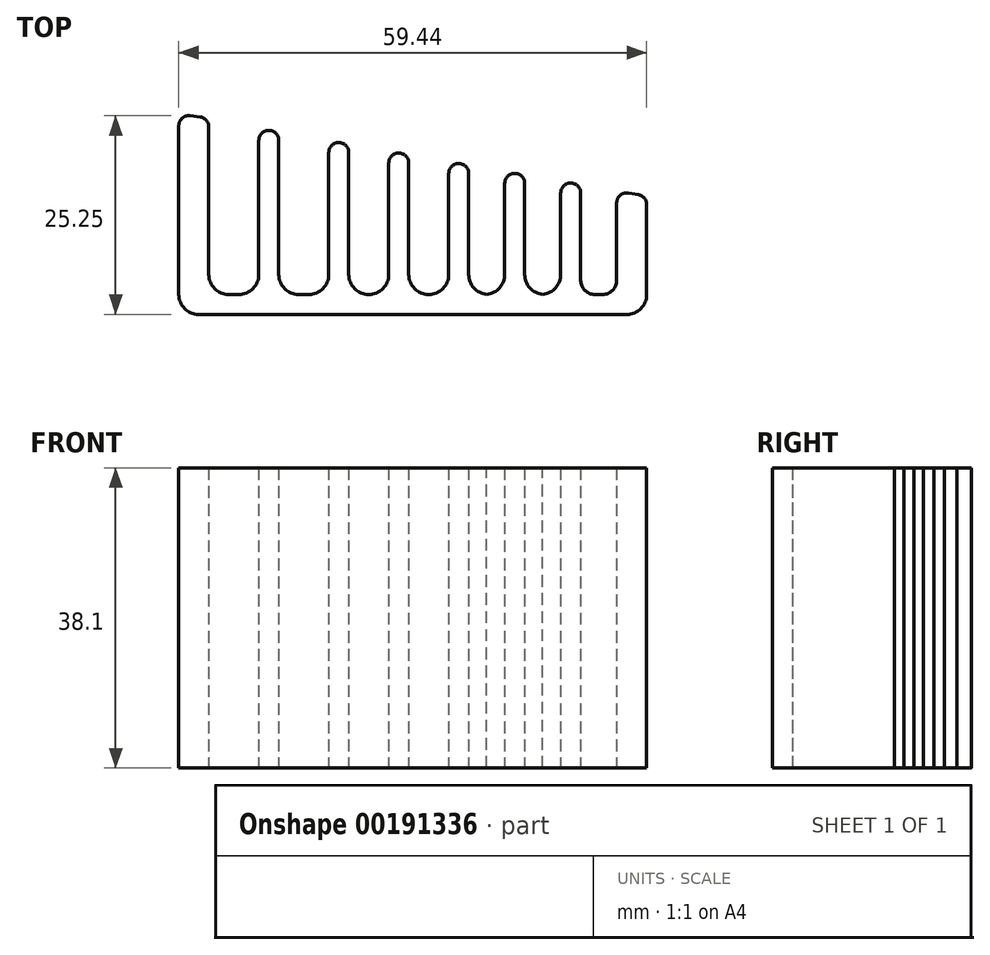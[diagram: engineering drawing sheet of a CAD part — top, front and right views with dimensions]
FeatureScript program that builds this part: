
annotation { "Feature Type Name" : "Feature", "Feature Type Description" : "" }
export const myFeature = defineFeature(function(context is Context, id is Id, definition is map)
    precondition{}
    {
        {
            var Q0;
            Q0=qCreatedBy(makeId("Top.planeOp"),FACE);
            var sketch = newSketch(context, id + "F0", { "sketchPlane" : qUnion([Q0])});
            skLineSegment(sketch, "E0", {"start": v(-36.35, 0) * mm, "end": v(36.35, 0) * mm});
            skPoint(sketch, "E1", {"position": v(0, 0) * mm});
            skLineSegment(sketch, "E2", {"start": v(-36.35, 0) * mm, "end": v(-36.35, 25.4) * mm});
            skLineSegment(sketch, "E3", {"start": v(36.35, 0) * mm, "end": v(36.35, 12.7) * mm});
            skPoint(sketch, "E4", {"position": v(-32.54, 24.98) * mm});
            skLineSegment(sketch, "E5", {"start": v(-36.35, 25.4) * mm, "end": v(-32.54, 24.98) * mm});
            skLineSegment(sketch, "E6", {"start": v(-32.54, 24.98) * mm, "end": v(-32.54, 2.54) * mm});
            skLineSegment(sketch, "E7", {"start": v(-36.35, 25.4) * mm, "end": v(36.35, 12.7) * mm, "construction": true});
            skLineSegment(sketch, "E8", {"start": v(-36.35, 2.54) * mm, "end": v(36.35, 2.54) * mm, "construction": true});
            skLineSegment(sketch, "E9", {"start": v(-26.19, 2.54) * mm, "end": v(-26.19, 23.63) * mm});
            skLineSegment(sketch, "E10", {"start": v(-26.19, 23.63) * mm, "end": v(-23.65, 23.18) * mm});
            skLineSegment(sketch, "E11", {"start": v(-23.65, 23.18) * mm, "end": v(-23.65, 2.54) * mm});
            skLineSegment(sketch, "E12", {"start": v(-23.65, 2.54) * mm, "end": v(-17.3, 2.54) * mm});
            skLineSegment(sketch, "E13", {"start": v(-17.3, 2.54) * mm, "end": v(-17.3, 22.07) * mm});
            skLineSegment(sketch, "E14", {"start": v(-17.3, 22.07) * mm, "end": v(-14.76, 21.63) * mm});
            skLineSegment(sketch, "E15", {"start": v(-14.76, 21.63) * mm, "end": v(-14.76, 2.54) * mm});
            skLineSegment(sketch, "E16", {"start": v(-14.76, 2.54) * mm, "end": v(-9.68, 2.54) * mm});
            skLineSegment(sketch, "E17", {"start": v(-9.68, 2.54) * mm, "end": v(-9.68, 20.74) * mm});
            skLineSegment(sketch, "E18", {"start": v(-9.68, 20.74) * mm, "end": v(-7.14, 20.3) * mm});
            skLineSegment(sketch, "E19", {"start": v(-7.14, 20.3) * mm, "end": v(-7.14, 2.54) * mm});
            skLineSegment(sketch, "E20", {"start": v(-7.14, 2.54) * mm, "end": v(-2.06, 2.54) * mm});
            skLineSegment(sketch, "E21", {"start": v(-2.06, 2.54) * mm, "end": v(-2.06, 19.4) * mm});
            skLineSegment(sketch, "E22", {"start": v(-2.06, 19.4) * mm, "end": v(0.48, 18.97) * mm});
            skLineSegment(sketch, "E23", {"start": v(0.48, 18.97) * mm, "end": v(0.48, 2.54) * mm});
            skLineSegment(sketch, "E24", {"start": v(0.48, 2.54) * mm, "end": v(5.05, 2.54) * mm});
            skLineSegment(sketch, "E25", {"start": v(5.05, 2.54) * mm, "end": v(5.05, 18.17) * mm});
            skLineSegment(sketch, "E26", {"start": v(5.05, 18.17) * mm, "end": v(7.6, 17.72) * mm});
            skLineSegment(sketch, "E27", {"start": v(7.6, 17.72) * mm, "end": v(7.6, 2.54) * mm});
            skLineSegment(sketch, "E28", {"start": v(7.6, 2.54) * mm, "end": v(12.17, 2.54) * mm});
            skLineSegment(sketch, "E29", {"start": v(12.17, 2.54) * mm, "end": v(12.17, 16.92) * mm});
            skLineSegment(sketch, "E30", {"start": v(12.17, 16.92) * mm, "end": v(14.7, 16.48) * mm});
            skLineSegment(sketch, "E31", {"start": v(14.7, 16.48) * mm, "end": v(14.7, 2.54) * mm});
            skLineSegment(sketch, "E32", {"start": v(14.7, 2.54) * mm, "end": v(19.28, 2.54) * mm});
            skLineSegment(sketch, "E33", {"start": v(19.28, 2.54) * mm, "end": v(19.28, 15.68) * mm});
            skLineSegment(sketch, "E34", {"start": v(19.28, 15.68) * mm, "end": v(23.09, 15.02) * mm});
            skLineSegment(sketch, "E35", {"start": v(23.09, 15.02) * mm, "end": v(23.09, 2.54) * mm});
            skLineSegment(sketch, "E36", {"start": v(23.09, 2.54) * mm, "end": v(26.8, 2.54) * mm});
            skLineSegment(sketch, "E37", {"start": v(26.8, 2.54) * mm, "end": v(26.8, 14.37) * mm});
            skLineSegment(sketch, "E38", {"start": v(26.8, 14.37) * mm, "end": v(29.34, 13.92) * mm});
            skLineSegment(sketch, "E39", {"start": v(29.34, 13.92) * mm, "end": v(29.34, 2.54) * mm});
            skLineSegment(sketch, "E40", {"start": v(29.34, 2.54) * mm, "end": v(32.54, 2.54) * mm});
            skLineSegment(sketch, "E41", {"start": v(32.54, 2.54) * mm, "end": v(32.54, 13.37) * mm});
            skLineSegment(sketch, "E42", {"start": v(32.54, 13.37) * mm, "end": v(36.35, 12.7) * mm});
            skLineSegment(sketch, "E43", {"start": v(-26.19, 2.54) * mm, "end": v(-32.54, 2.54) * mm});
            skSolve(sketch);
        }
        {
            var Q0;
            Q0=qSketchRegion(id+"F0",true);
            extrude(context, id + "F1", {"entities" : qUnion([Q0]), "depth" : 38.1 * mm});
        }
        {
            var Q0;
            Q0=makeQuery(id+"F1.opExtrude","SWEPT_EDGE",EDGE,{"disambiguationData":[OSD([sQuery(id+"F0.wireOp",EDGE,"E6"),sQuery(id+"F0.wireOp",EDGE,"E43")])]});
            var Q1;
            Q1=makeQuery(id+"F1.opExtrude","SWEPT_EDGE",EDGE,{"disambiguationData":[OSD([sQuery(id+"F0.wireOp",EDGE,"E9"),sQuery(id+"F0.wireOp",EDGE,"E43")])]});
            var Q2;
            Q2=makeQuery(id+"F1.opExtrude","SWEPT_EDGE",EDGE,{"disambiguationData":[OSD([sQuery(id+"F0.wireOp",EDGE,"E11"),sQuery(id+"F0.wireOp",EDGE,"E12")])]});
            var Q3;
            Q3=makeQuery(id+"F1.opExtrude","SWEPT_EDGE",EDGE,{"disambiguationData":[OSD([sQuery(id+"F0.wireOp",EDGE,"E12"),sQuery(id+"F0.wireOp",EDGE,"E13")])]});
            var Q4;
            Q4=makeQuery(id+"F1.opExtrude","SWEPT_EDGE",EDGE,{"disambiguationData":[OSD([sQuery(id+"F0.wireOp",EDGE,"E15"),sQuery(id+"F0.wireOp",EDGE,"E16")])]});
            var Q5;
            Q5=makeQuery(id+"F1.opExtrude","SWEPT_EDGE",EDGE,{"disambiguationData":[OSD([sQuery(id+"F0.wireOp",EDGE,"E16"),sQuery(id+"F0.wireOp",EDGE,"E17")])]});
            var Q6;
            Q6=makeQuery(id+"F1.opExtrude","SWEPT_EDGE",EDGE,{"disambiguationData":[OSD([sQuery(id+"F0.wireOp",EDGE,"E19"),sQuery(id+"F0.wireOp",EDGE,"E20")])]});
            var Q7;
            Q7=makeQuery(id+"F1.opExtrude","SWEPT_EDGE",EDGE,{"disambiguationData":[OSD([sQuery(id+"F0.wireOp",EDGE,"E20"),sQuery(id+"F0.wireOp",EDGE,"E21")])]});
            var Q8;
            Q8=makeQuery(id+"F1.opExtrude","SWEPT_EDGE",EDGE,{"disambiguationData":[OSD([sQuery(id+"F0.wireOp",EDGE,"E23"),sQuery(id+"F0.wireOp",EDGE,"E24")])]});
            var Q9;
            Q9=makeQuery(id+"F1.opExtrude","SWEPT_EDGE",EDGE,{"disambiguationData":[OSD([sQuery(id+"F0.wireOp",EDGE,"E24"),sQuery(id+"F0.wireOp",EDGE,"E25")])]});
            var Q10;
            Q10=makeQuery(id+"F1.opExtrude","SWEPT_EDGE",EDGE,{"disambiguationData":[OSD([sQuery(id+"F0.wireOp",EDGE,"E27"),sQuery(id+"F0.wireOp",EDGE,"E28")])]});
            var Q11;
            Q11=makeQuery(id+"F1.opExtrude","SWEPT_EDGE",EDGE,{"disambiguationData":[OSD([sQuery(id+"F0.wireOp",EDGE,"E28"),sQuery(id+"F0.wireOp",EDGE,"E29")])]});
            var Q12;
            Q12=makeQuery(id+"F1.opExtrude","SWEPT_EDGE",EDGE,{"disambiguationData":[OSD([sQuery(id+"F0.wireOp",EDGE,"E0"),sQuery(id+"F0.wireOp",EDGE,"E2")])]});
            var Q13;
            Q13=makeQuery(id+"F1.opExtrude","SWEPT_EDGE",EDGE,{"disambiguationData":[OSD([sQuery(id+"F0.wireOp",EDGE,"E0"),sQuery(id+"F0.wireOp",EDGE,"E3")])]});
            fillet(context, id + "F2", {"entities" : qUnion([Q0, Q1, Q2, Q3, Q4, Q5, Q6, Q7, Q8, Q9, Q10, Q11, Q12, Q13]), "radius" : 2.54 * mm, "tangentPropagation" : true, "allowEdgeOverflow" : false});
        }
        {
            var Q0;
            Q0=makeQuery(id+"F1.opExtrude","SWEPT_EDGE",EDGE,{"disambiguationData":[OSD([sQuery(id+"F0.wireOp",EDGE,"E31"),sQuery(id+"F0.wireOp",EDGE,"E32")])]});
            var Q1;
            Q1=makeQuery(id+"F1.opExtrude","SWEPT_EDGE",EDGE,{"disambiguationData":[OSD([sQuery(id+"F0.wireOp",EDGE,"E32"),sQuery(id+"F0.wireOp",EDGE,"E33")])]});
            var Q2;
            Q2=makeQuery(id+"F1.opExtrude","SWEPT_EDGE",EDGE,{"disambiguationData":[OSD([sQuery(id+"F0.wireOp",EDGE,"E35"),sQuery(id+"F0.wireOp",EDGE,"E36")])]});
            var Q3;
            Q3=makeQuery(id+"F1.opExtrude","SWEPT_EDGE",EDGE,{"disambiguationData":[OSD([sQuery(id+"F0.wireOp",EDGE,"E36"),sQuery(id+"F0.wireOp",EDGE,"E37")])]});
            var Q4;
            Q4=makeQuery(id+"F1.opExtrude","SWEPT_EDGE",EDGE,{"disambiguationData":[OSD([sQuery(id+"F0.wireOp",EDGE,"E39"),sQuery(id+"F0.wireOp",EDGE,"E40")])]});
            var Q5;
            Q5=makeQuery(id+"F1.opExtrude","SWEPT_EDGE",EDGE,{"disambiguationData":[OSD([sQuery(id+"F0.wireOp",EDGE,"E40"),sQuery(id+"F0.wireOp",EDGE,"E41")])]});
            fillet(context, id + "F3", {"entities" : qUnion([Q0, Q1, Q2, Q3, Q4, Q5]), "radius" : 1.78 * mm, "tangentPropagation" : true, "allowEdgeOverflow" : false});
        }
        {
            var Q0;
            Q0=makeQuery(id+"F1.opExtrude","SWEPT_EDGE",EDGE,{"disambiguationData":[OSD([sQuery(id+"F0.wireOp",EDGE,"E41"),sQuery(id+"F0.wireOp",EDGE,"E42")])]});
            var Q1;
            Q1=makeQuery(id+"F1.opExtrude","SWEPT_EDGE",EDGE,{"disambiguationData":[OSD([sQuery(id+"F0.wireOp",EDGE,"E38"),sQuery(id+"F0.wireOp",EDGE,"E39")])]});
            var Q2;
            Q2=makeQuery(id+"F1.opExtrude","SWEPT_EDGE",EDGE,{"disambiguationData":[OSD([sQuery(id+"F0.wireOp",EDGE,"E37"),sQuery(id+"F0.wireOp",EDGE,"E38")])]});
            var Q3;
            Q3=makeQuery(id+"F1.opExtrude","SWEPT_EDGE",EDGE,{"disambiguationData":[OSD([sQuery(id+"F0.wireOp",EDGE,"E34"),sQuery(id+"F0.wireOp",EDGE,"E35")])]});
            var Q4;
            Q4=makeQuery(id+"F1.opExtrude","SWEPT_EDGE",EDGE,{"disambiguationData":[OSD([sQuery(id+"F0.wireOp",EDGE,"E33"),sQuery(id+"F0.wireOp",EDGE,"E34")])]});
            var Q5;
            Q5=makeQuery(id+"F1.opExtrude","SWEPT_EDGE",EDGE,{"disambiguationData":[OSD([sQuery(id+"F0.wireOp",EDGE,"E30"),sQuery(id+"F0.wireOp",EDGE,"E31")])]});
            var Q6;
            Q6=makeQuery(id+"F1.opExtrude","SWEPT_EDGE",EDGE,{"disambiguationData":[OSD([sQuery(id+"F0.wireOp",EDGE,"E29"),sQuery(id+"F0.wireOp",EDGE,"E30")])]});
            var Q7;
            Q7=makeQuery(id+"F1.opExtrude","SWEPT_EDGE",EDGE,{"disambiguationData":[OSD([sQuery(id+"F0.wireOp",EDGE,"E26"),sQuery(id+"F0.wireOp",EDGE,"E27")])]});
            var Q8;
            Q8=makeQuery(id+"F1.opExtrude","SWEPT_EDGE",EDGE,{"disambiguationData":[OSD([sQuery(id+"F0.wireOp",EDGE,"E25"),sQuery(id+"F0.wireOp",EDGE,"E26")])]});
            var Q9;
            Q9=makeQuery(id+"F1.opExtrude","SWEPT_EDGE",EDGE,{"disambiguationData":[OSD([sQuery(id+"F0.wireOp",EDGE,"E22"),sQuery(id+"F0.wireOp",EDGE,"E23")])]});
            var Q10;
            Q10=makeQuery(id+"F1.opExtrude","SWEPT_EDGE",EDGE,{"disambiguationData":[OSD([sQuery(id+"F0.wireOp",EDGE,"E21"),sQuery(id+"F0.wireOp",EDGE,"E22")])]});
            var Q11;
            Q11=makeQuery(id+"F1.opExtrude","SWEPT_EDGE",EDGE,{"disambiguationData":[OSD([sQuery(id+"F0.wireOp",EDGE,"E18"),sQuery(id+"F0.wireOp",EDGE,"E19")])]});
            var Q12;
            Q12=makeQuery(id+"F1.opExtrude","SWEPT_EDGE",EDGE,{"disambiguationData":[OSD([sQuery(id+"F0.wireOp",EDGE,"E14"),sQuery(id+"F0.wireOp",EDGE,"E15")])]});
            var Q13;
            Q13=makeQuery(id+"F1.opExtrude","SWEPT_EDGE",EDGE,{"disambiguationData":[OSD([sQuery(id+"F0.wireOp",EDGE,"E10"),sQuery(id+"F0.wireOp",EDGE,"E11")])]});
            var Q14;
            Q14=makeQuery(id+"F1.opExtrude","SWEPT_EDGE",EDGE,{"disambiguationData":[OSD([sQuery(id+"F0.wireOp",EDGE,"E9"),sQuery(id+"F0.wireOp",EDGE,"E10")])]});
            var Q15;
            Q15=makeQuery(id+"F1.opExtrude","SWEPT_EDGE",EDGE,{"disambiguationData":[OSD([sQuery(id+"F0.wireOp",EDGE,"E5"),sQuery(id+"F0.wireOp",EDGE,"E6")])]});
            var Q16;
            Q16=makeQuery(id+"F1.opExtrude","SWEPT_EDGE",EDGE,{"disambiguationData":[OSD([sQuery(id+"F0.wireOp",EDGE,"E2"),sQuery(id+"F0.wireOp",EDGE,"E5")])]});
            var Q17;
            Q17=makeQuery(id+"F1.opExtrude","SWEPT_EDGE",EDGE,{"disambiguationData":[OSD([sQuery(id+"F0.wireOp",EDGE,"E3"),sQuery(id+"F0.wireOp",EDGE,"E42")])]});
            var Q18;
            Q18=makeQuery(id+"F1.opExtrude","SWEPT_EDGE",EDGE,{"disambiguationData":[OSD([sQuery(id+"F0.wireOp",EDGE,"E17"),sQuery(id+"F0.wireOp",EDGE,"E18")])]});
            var Q19;
            Q19=makeQuery(id+"F1.opExtrude","SWEPT_EDGE",EDGE,{"disambiguationData":[OSD([sQuery(id+"F0.wireOp",EDGE,"E13"),sQuery(id+"F0.wireOp",EDGE,"E14")])]});
            fillet(context, id + "F4", {"entities" : qUnion([Q0, Q1, Q2, Q3, Q4, Q5, Q6, Q7, Q8, Q9, Q10, Q11, Q12, Q13, Q14, Q15, Q16, Q17, Q18, Q19]), "radius" : 1.27 * mm, "tangentPropagation" : true, "allowEdgeOverflow" : false});
        }
        {
            var Q0;
            Q0=makeQuery(id+"F1.opExtrude","CAP_FACE",FACE,{"disambiguationData":[OSD([sQuery(id+"F0.wireOp",EDGE,"E0"),sQuery(id+"F0.wireOp",EDGE,"E2"),sQuery(id+"F0.wireOp",EDGE,"E3"),sQuery(id+"F0.wireOp",EDGE,"E5"),sQuery(id+"F0.wireOp",EDGE,"E6"),sQuery(id+"F0.wireOp",EDGE,"E9"),sQuery(id+"F0.wireOp",EDGE,"E10"),sQuery(id+"F0.wireOp",EDGE,"E11"),sQuery(id+"F0.wireOp",EDGE,"E12"),sQuery(id+"F0.wireOp",EDGE,"E13"),sQuery(id+"F0.wireOp",EDGE,"E14"),sQuery(id+"F0.wireOp",EDGE,"E15"),sQuery(id+"F0.wireOp",EDGE,"E16"),sQuery(id+"F0.wireOp",EDGE,"E17"),sQuery(id+"F0.wireOp",EDGE,"E18"),sQuery(id+"F0.wireOp",EDGE,"E19"),sQuery(id+"F0.wireOp",EDGE,"E20"),sQuery(id+"F0.wireOp",EDGE,"E21"),sQuery(id+"F0.wireOp",EDGE,"E22"),sQuery(id+"F0.wireOp",EDGE,"E23"),sQuery(id+"F0.wireOp",EDGE,"E24"),sQuery(id+"F0.wireOp",EDGE,"E25"),sQuery(id+"F0.wireOp",EDGE,"E26"),sQuery(id+"F0.wireOp",EDGE,"E27"),sQuery(id+"F0.wireOp",EDGE,"E28"),sQuery(id+"F0.wireOp",EDGE,"E29"),sQuery(id+"F0.wireOp",EDGE,"E30"),sQuery(id+"F0.wireOp",EDGE,"E31"),sQuery(id+"F0.wireOp",EDGE,"E32"),sQuery(id+"F0.wireOp",EDGE,"E33"),sQuery(id+"F0.wireOp",EDGE,"E34"),sQuery(id+"F0.wireOp",EDGE,"E35"),sQuery(id+"F0.wireOp",EDGE,"E36"),sQuery(id+"F0.wireOp",EDGE,"E37"),sQuery(id+"F0.wireOp",EDGE,"E38"),sQuery(id+"F0.wireOp",EDGE,"E39"),sQuery(id+"F0.wireOp",EDGE,"E40"),sQuery(id+"F0.wireOp",EDGE,"E41"),sQuery(id+"F0.wireOp",EDGE,"E42"),sQuery(id+"F0.wireOp",EDGE,"E43")])],"isStart":false});
            var sketch = newSketch(context, id + "F5", { "sketchPlane" : qUnion([Q0])});
            skLineSegment(sketch, "E44.0.0", {"start": v(36.35, 2.54) * mm, "end": v(36.35, 11.63) * mm, "construction": true});
            skArc(sketch, "E44.0.1", {"start": v(36.35, 11.63) * mm, "mid": v(36.05, 12.45) * mm, "end": v(35.3, 12.88) * mm, "construction": true});
            skLineSegment(sketch, "E44.0.2", {"start": v(35.3, 12.88) * mm, "end": v(34.03, 13.1) * mm, "construction": true});
            skArc(sketch, "E44.0.3", {"start": v(34.03, 13.1) * mm, "mid": v(33, 12.83) * mm, "end": v(32.54, 11.85) * mm, "construction": true});
            skLineSegment(sketch, "E44.0.4", {"start": v(32.54, 11.85) * mm, "end": v(32.54, 4.32) * mm, "construction": true});
            skArc(sketch, "E44.0.5", {"start": v(32.54, 4.32) * mm, "mid": v(32.08, 3.13) * mm, "end": v(30.94, 2.55) * mm, "construction": true});
            skArc(sketch, "E44.0.6", {"start": v(30.94, 2.55) * mm, "mid": v(29.8, 3.13) * mm, "end": v(29.34, 4.32) * mm, "construction": true});
            skLineSegment(sketch, "E44.0.7", {"start": v(29.34, 4.32) * mm, "end": v(29.34, 12.86) * mm, "construction": true});
            skArc(sketch, "E44.0.8", {"start": v(29.34, 12.86) * mm, "mid": v(28.07, 14.13) * mm, "end": v(26.8, 12.86) * mm, "construction": true});
            skLineSegment(sketch, "E44.0.9", {"start": v(26.8, 12.86) * mm, "end": v(26.8, 4.32) * mm, "construction": true});
            skArc(sketch, "E44.0.10", {"start": v(26.8, 4.32) * mm, "mid": v(26.28, 3.06) * mm, "end": v(25.02, 2.54) * mm, "construction": true});
            skLineSegment(sketch, "E44.0.11", {"start": v(25.02, 2.54) * mm, "end": v(24.87, 2.54) * mm, "construction": true});
            skArc(sketch, "E44.0.12", {"start": v(24.87, 2.54) * mm, "mid": v(23.6, 3.06) * mm, "end": v(23.09, 4.32) * mm, "construction": true});
            skLineSegment(sketch, "E44.0.13", {"start": v(23.09, 4.32) * mm, "end": v(23.09, 13.95) * mm, "construction": true});
            skArc(sketch, "E44.0.14", {"start": v(23.09, 13.95) * mm, "mid": v(22.8, 14.77) * mm, "end": v(22.04, 15.2) * mm, "construction": true});
            skLineSegment(sketch, "E44.0.15", {"start": v(22.04, 15.2) * mm, "end": v(20.77, 15.42) * mm, "construction": true});
            skArc(sketch, "E44.0.16", {"start": v(20.77, 15.42) * mm, "mid": v(19.73, 15.14) * mm, "end": v(19.28, 14.17) * mm, "construction": true});
            skLineSegment(sketch, "E44.0.17", {"start": v(19.28, 14.17) * mm, "end": v(19.28, 4.32) * mm, "construction": true});
            skArc(sketch, "E44.0.18", {"start": v(19.28, 4.32) * mm, "mid": v(18.76, 3.06) * mm, "end": v(17.5, 2.54) * mm, "construction": true});
            skLineSegment(sketch, "E44.0.19", {"start": v(17.5, 2.54) * mm, "end": v(16.48, 2.54) * mm, "construction": true});
            skArc(sketch, "E44.0.20", {"start": v(16.48, 2.54) * mm, "mid": v(15.23, 3.06) * mm, "end": v(14.7, 4.32) * mm, "construction": true});
            skLineSegment(sketch, "E44.0.21", {"start": v(14.7, 4.32) * mm, "end": v(14.7, 15.41) * mm, "construction": true});
            skArc(sketch, "E44.0.22", {"start": v(14.7, 15.41) * mm, "mid": v(13.44, 16.68) * mm, "end": v(12.17, 15.41) * mm, "construction": true});
            skLineSegment(sketch, "E44.0.23", {"start": v(12.17, 15.41) * mm, "end": v(12.17, 5.08) * mm, "construction": true});
            skArc(sketch, "E44.0.24", {"start": v(12.17, 5.08) * mm, "mid": v(11.51, 3.38) * mm, "end": v(9.88, 2.55) * mm, "construction": true});
            skArc(sketch, "E44.0.25", {"start": v(9.88, 2.55) * mm, "mid": v(8.25, 3.38) * mm, "end": v(7.6, 5.08) * mm, "construction": true});
            skLineSegment(sketch, "E44.0.26", {"start": v(7.6, 5.08) * mm, "end": v(7.6, 16.66) * mm, "construction": true});
            skArc(sketch, "E44.0.27", {"start": v(7.6, 16.66) * mm, "mid": v(6.32, 17.93) * mm, "end": v(5.05, 16.66) * mm, "construction": true});
            skLineSegment(sketch, "E44.0.28", {"start": v(5.05, 16.66) * mm, "end": v(5.05, 5.08) * mm, "construction": true});
            skArc(sketch, "E44.0.29", {"start": v(5.05, 5.08) * mm, "mid": v(4.4, 3.38) * mm, "end": v(2.77, 2.55) * mm, "construction": true});
            skArc(sketch, "E44.0.30", {"start": v(2.77, 2.55) * mm, "mid": v(1.14, 3.38) * mm, "end": v(0.48, 5.08) * mm, "construction": true});
            skLineSegment(sketch, "E44.0.31", {"start": v(0.48, 5.08) * mm, "end": v(0.48, 17.9) * mm, "construction": true});
            skArc(sketch, "E44.0.32", {"start": v(0.48, 17.9) * mm, "mid": v(-0.79, 19.17) * mm, "end": v(-2.06, 17.9) * mm, "construction": true});
            skLineSegment(sketch, "E44.0.33", {"start": v(-2.06, 17.9) * mm, "end": v(-2.06, 5.08) * mm, "construction": true});
            skArc(sketch, "E44.0.34", {"start": v(-2.06, 5.08) * mm, "mid": v(-4.6, 2.54) * mm, "end": v(-7.14, 5.08) * mm, "construction": true});
            skLineSegment(sketch, "E44.0.35", {"start": v(-7.14, 5.08) * mm, "end": v(-7.14, 19.23) * mm, "construction": true});
            skArc(sketch, "E44.0.36", {"start": v(-7.14, 19.23) * mm, "mid": v(-8.4, 20.5) * mm, "end": v(-9.68, 19.23) * mm, "construction": true});
            skLineSegment(sketch, "E44.0.37", {"start": v(-9.68, 19.23) * mm, "end": v(-9.68, 5.08) * mm, "construction": true});
            skArc(sketch, "E44.0.38", {"start": v(-9.68, 5.08) * mm, "mid": v(-12.22, 2.54) * mm, "end": v(-14.76, 5.08) * mm, "construction": true});
            skLineSegment(sketch, "E44.0.39", {"start": v(-14.76, 5.08) * mm, "end": v(-14.76, 20.56) * mm, "construction": true});
            skArc(sketch, "E44.0.40", {"start": v(-14.76, 20.56) * mm, "mid": v(-16.03, 21.83) * mm, "end": v(-17.3, 20.56) * mm, "construction": true});
            skLineSegment(sketch, "E44.0.41", {"start": v(-17.3, 20.56) * mm, "end": v(-17.3, 5.08) * mm, "construction": true});
            skArc(sketch, "E44.0.42", {"start": v(-17.3, 5.08) * mm, "mid": v(-18.04, 3.28) * mm, "end": v(-19.84, 2.54) * mm, "construction": true});
            skLineSegment(sketch, "E44.0.43", {"start": v(-19.84, 2.54) * mm, "end": v(-21.1, 2.54) * mm, "construction": true});
            skArc(sketch, "E44.0.44", {"start": v(-21.1, 2.54) * mm, "mid": v(-22.9, 3.28) * mm, "end": v(-23.65, 5.08) * mm, "construction": true});
            skLineSegment(sketch, "E44.0.45", {"start": v(-23.65, 5.08) * mm, "end": v(-23.65, 22.11) * mm, "construction": true});
            skArc(sketch, "E44.0.46", {"start": v(-23.65, 22.11) * mm, "mid": v(-24.92, 23.38) * mm, "end": v(-26.19, 22.11) * mm, "construction": true});
            skLineSegment(sketch, "E44.0.47", {"start": v(-26.19, 22.11) * mm, "end": v(-26.19, 5.08) * mm, "construction": true});
            skArc(sketch, "E44.0.48", {"start": v(-26.19, 5.08) * mm, "mid": v(-26.93, 3.28) * mm, "end": v(-28.73, 2.54) * mm, "construction": true});
            skLineSegment(sketch, "E44.0.49", {"start": v(-28.73, 2.54) * mm, "end": v(-30, 2.54) * mm, "construction": true});
            skArc(sketch, "E44.0.50", {"start": v(-30, 2.54) * mm, "mid": v(-31.8, 3.28) * mm, "end": v(-32.54, 5.08) * mm, "construction": true});
            skLineSegment(sketch, "E44.0.51", {"start": v(-32.54, 5.08) * mm, "end": v(-32.54, 23.84) * mm, "construction": true});
            skArc(sketch, "E44.0.52", {"start": v(-32.54, 23.84) * mm, "mid": v(-32.86, 24.69) * mm, "end": v(-33.67, 25.1) * mm, "construction": true});
            skLineSegment(sketch, "E44.0.53", {"start": v(-33.67, 25.1) * mm, "end": v(-34.94, 25.24) * mm, "construction": true});
            skArc(sketch, "E44.0.54", {"start": v(-34.94, 25.24) * mm, "mid": v(-35.92, 24.93) * mm, "end": v(-36.35, 23.98) * mm, "construction": true});
            skLineSegment(sketch, "E44.0.55", {"start": v(-36.35, 23.98) * mm, "end": v(-36.35, 2.54) * mm, "construction": true});
            skArc(sketch, "E44.0.56", {"start": v(-36.35, 2.54) * mm, "mid": v(-35.6, 0.74) * mm, "end": v(-33.8, 0) * mm, "construction": true});
            skLineSegment(sketch, "E44.0.57", {"start": v(-33.8, 0) * mm, "end": v(33.8, 0) * mm, "construction": true});
            skArc(sketch, "E44.0.58", {"start": v(33.8, 0) * mm, "mid": v(35.6, 0.74) * mm, "end": v(36.35, 2.54) * mm, "construction": true});
            skLineSegment(sketch, "E45.bottom", {"start": v(23.09, 13.95) * mm, "end": v(53.08, 13.95) * mm});
            skLineSegment(sketch, "E45.top", {"start": v(23.09, -14.55) * mm, "end": v(53.08, -14.55) * mm});
            skLineSegment(sketch, "E45.left", {"start": v(23.09, 13.95) * mm, "end": v(23.09, -14.55) * mm});
            skLineSegment(sketch, "E45.right", {"start": v(53.08, 13.95) * mm, "end": v(53.08, -14.55) * mm});
            skLineSegment(sketch, "E46.bottom", {"start": v(23.09, 13.95) * mm, "end": v(46.76, 13.95) * mm});
            skLineSegment(sketch, "E46.top", {"start": v(23.09, 25.24) * mm, "end": v(46.76, 25.24) * mm});
            skLineSegment(sketch, "E46.left", {"start": v(23.09, 13.95) * mm, "end": v(23.09, 25.24) * mm});
            skLineSegment(sketch, "E46.right", {"start": v(46.76, 13.95) * mm, "end": v(46.76, 25.24) * mm});
            skSolve(sketch);
        }
        {
            var Q0;
            Q0 = qSketchRegion(id + "F5", true);
            extrude(context, id + "F6", {"entities" : qUnion([Q0]), "operationType" : NewBodyOperationType.REMOVE, "endBound" : BoundingType.THROUGH_ALL, "oppositeDirection" : true, "depth" : 25.4 * mm});
        }
        {
            var Q0;
            Q0=makeQuery(id+"F6.boolean.opBoolean","INTERSECT",EDGE,{"derivedFrom":[makeQuery(id+"F1.opExtrude","SWEPT_FACE",FACE,{"disambiguationData":[OSD([sQuery(id+"F0.wireOp",EDGE,"E0")])]}),makeQuery(id+"F6.opExtrude","SWEPT_FACE",FACE,{"disambiguationData":[OSD([sQuery(id+"F5.wireOp",EDGE,"E45.left"),sQuery(id+"F5.wireOp",EDGE,"E46.left")])]})]});
            fillet(context, id + "F7", {"entities" : qUnion([Q0]), "radius" : 2.54 * mm, "tangentPropagation" : true, "allowEdgeOverflow" : false});
        }
    });
